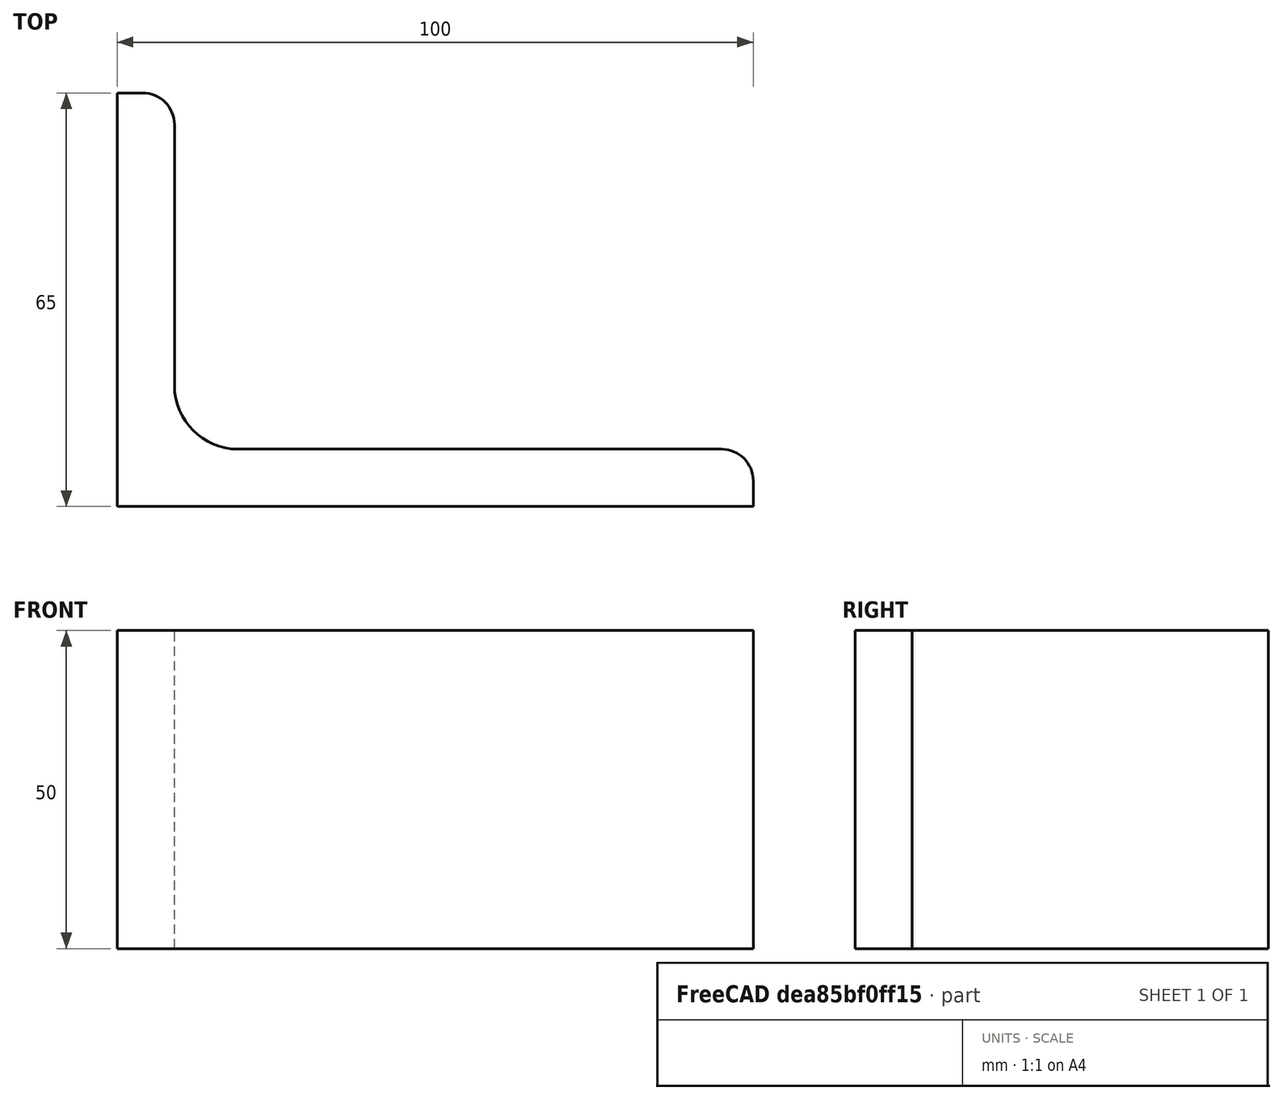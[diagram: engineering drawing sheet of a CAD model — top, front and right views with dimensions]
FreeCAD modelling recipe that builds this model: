
FCSTD DOCUMENT  (FreeCAD 0.15R4671 (Git))
Label: Angle Bar 100x65x9 EN10056 S235JR
License: All rights reserved
LicenseURL: http://en.wikipedia.org/wiki/All_rights_reserved
objects: Sketcher::SketchObject×1, Part::Extrusion×1
note: 2 computed .brp shape members not serialized (recipe doc carries the construction recipe); baked Part::Feature solids carry a one-line shape summary decoded from their .brp

FEATURE [Sketcher::SketchObject] Sketch
  sketch-geometry (9):
    g0: LineSegment StartX=0 StartY=0 StartZ=0 EndX=100 EndY=0 EndZ=0
    g1: LineSegment StartX=100 StartY=0 StartZ=0 EndX=100 EndY=4 EndZ=0
    g2: LineSegment StartX=95 StartY=9 StartZ=0 EndX=19 EndY=9 EndZ=0
    g3: LineSegment StartX=0 StartY=0 StartZ=0 EndX=0 EndY=65 EndZ=0
    g4: LineSegment StartX=0 StartY=65 StartZ=0 EndX=4 EndY=65 EndZ=0
    g5: LineSegment StartX=9 StartY=60 StartZ=0 EndX=9 EndY=19 EndZ=0
    g6: ArcOfCircle CenterX=19 CenterY=19 CenterZ=0 NormalX=0 NormalY=0 NormalZ=1 Radius=10 StartAngle=3.14159 EndAngle=4.71239
    g7: ArcOfCircle CenterX=4 CenterY=60 CenterZ=0 NormalX=0 NormalY=0 NormalZ=1 Radius=5 StartAngle=0 EndAngle=1.5708
    g8: ArcOfCircle CenterX=95 CenterY=4 CenterZ=0 NormalX=0 NormalY=0 NormalZ=1 Radius=5 StartAngle=0 EndAngle=1.5708
  constraints (23):
    c: Coincident(g0,g-1)
    c: Horizontal(g0)
    c: Coincident(g1,g0)
    c: Vertical(g1)
    c: Horizontal(g2)
    c: Coincident(g3,g-1)
    c: Vertical(g3)
    c: Coincident(g4,g3)
    c: Horizontal(g4)
    c: Vertical(g5)
    c: Tangent(g5,g6) = -1.5708
    c: Tangent(g2,g6) = 1.5708
    c: Tangent(g4,g7) = 1.5708
    c: Tangent(g5,g7) = 1.5708
    c: Tangent(g2,g8) = -1.5708
    c: Tangent(g1,g8) = -1.5708
    c: DistanceX(g0) = 100
    c: DistanceY(g3) = 65
    c: DistanceY(g0,g2) = 9
    c: DistanceX(g3,g5) = 9
    c: Radius(g6) = 10
    c: Radius(g8) = 5
    c: Radius(g7) = 5
FEATURE [Part::Extrusion] Extrude  label="Angle Bar 100x65x9 EN10056 S235JR"
  Base = -> Sketch
  Dir = (0,0,50)
  Solid = true
